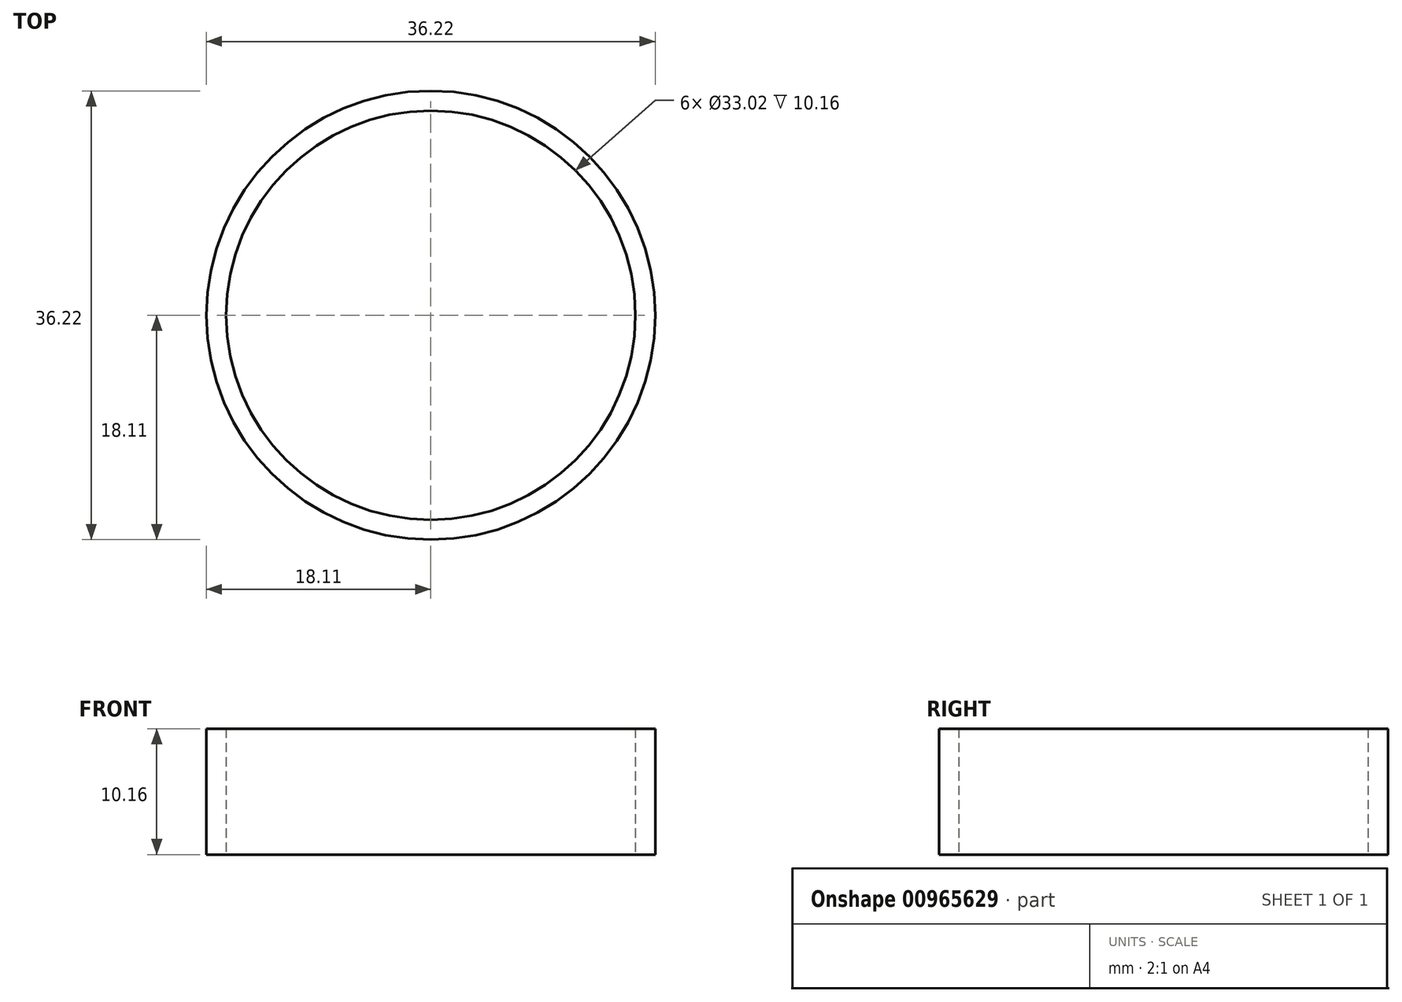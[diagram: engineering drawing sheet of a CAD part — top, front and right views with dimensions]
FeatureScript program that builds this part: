
annotation { "Feature Type Name" : "Feature", "Feature Type Description" : "" }
export const myFeature = defineFeature(function(context is Context, id is Id, definition is map)
    precondition{}
    {
        {
            var Q0;
            Q0=qCreatedBy(makeId("Top.planeOp"),FACE);
            var sketch = newSketch(context, id + "F0", { "sketchPlane" : qUnion([Q0])});
            skCircle(sketch, "E0", {"center": v(0, 0) * mm, "radius": 16.51 * mm});
            skCircle(sketch, "E1", {"center": v(0, 0) * mm, "radius": 18.11 * mm});
            skLineSegment(sketch, "E2", {"start": v(0, -16.51) * mm, "end": v(0, -18.11) * mm});
            skSolve(sketch);
        }
        {
            var Q0;
            Q0 = qSketchRegion(id + "F0", true);
            extrude(context, id + "F1", {"entities" : qUnion([Q0]), "depth" : 10.16 * mm, "offsetDistance" : 25.4 * mm});
        }
    });
